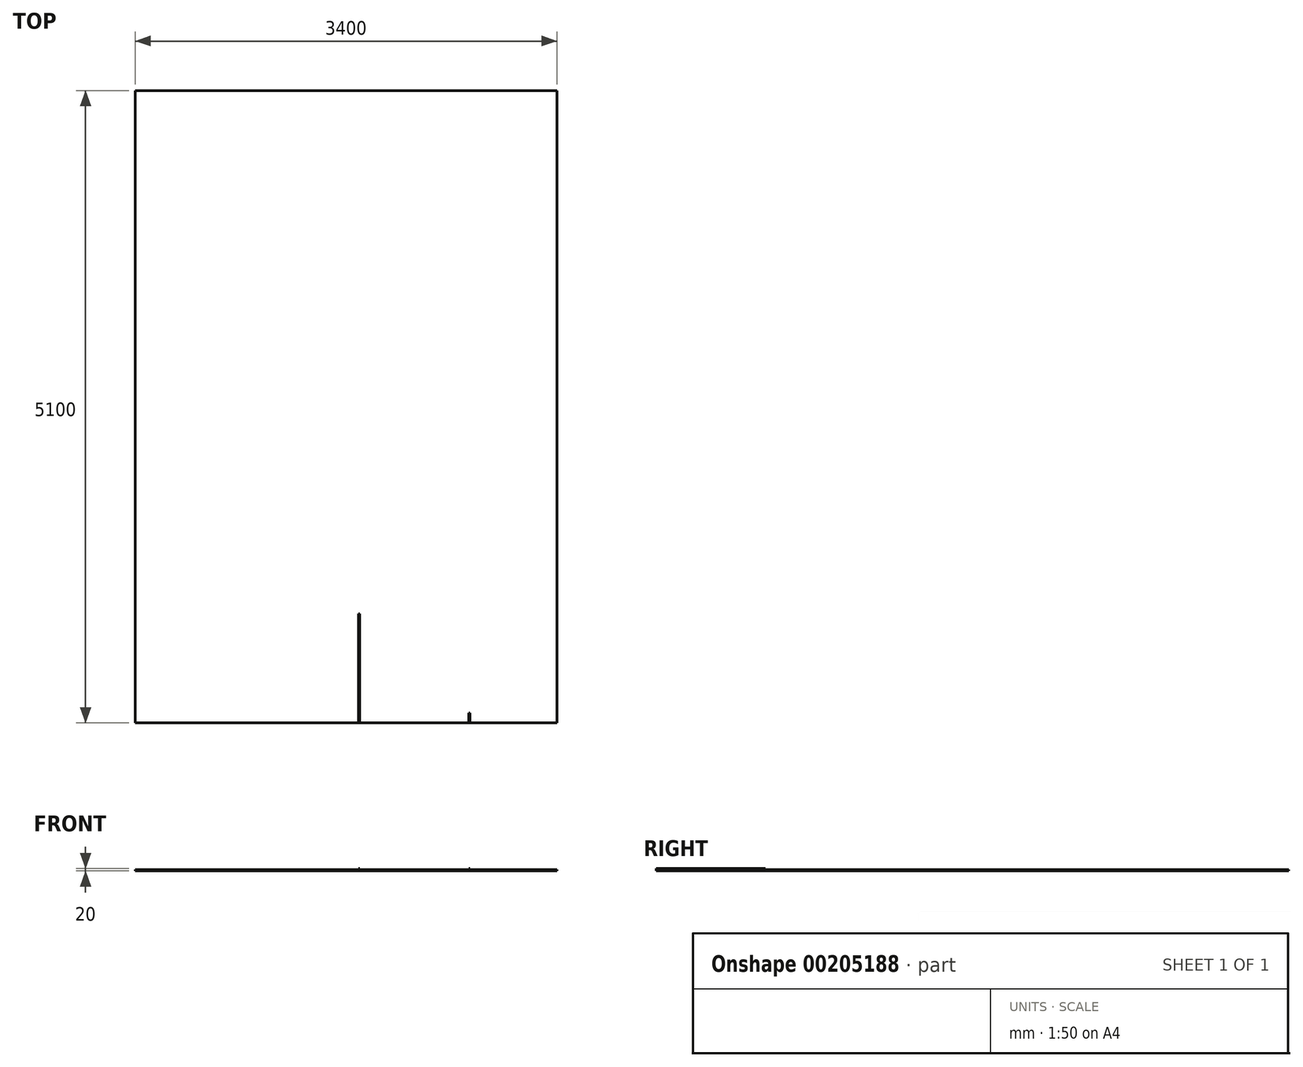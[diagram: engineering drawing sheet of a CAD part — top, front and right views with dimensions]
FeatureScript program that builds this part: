
annotation { "Feature Type Name" : "Feature", "Feature Type Description" : "" }
export const myFeature = defineFeature(function(context is Context, id is Id, definition is map)
    precondition{}
    {
        {
            var Q0;
            Q0=qCreatedBy(makeId("Top.planeOp"),FACE);
            var sketch = newSketch(context, id + "F0", { "sketchPlane" : qUnion([Q0])});
            skLineSegment(sketch, "E0.bottom", {"start": v(1700, 2550) * mm, "end": v(-1700, 2550) * mm});
            skLineSegment(sketch, "E0.top", {"start": v(1700, -2550) * mm, "end": v(-1700, -2550) * mm});
            skLineSegment(sketch, "E0.left", {"start": v(1700, 2550) * mm, "end": v(1700, -2550) * mm});
            skLineSegment(sketch, "E0.right", {"start": v(-1700, 2550) * mm, "end": v(-1700, -2550) * mm});
            skPoint(sketch, "E0.middle", {"position": v(0, 0) * mm});
            skSolve(sketch);
        }
        {
            var Q0;
            Q0 = qSketchRegion(id + "F0", true);
            extrude(context, id + "F1", {"entities" : qUnion([Q0]), "depth" : 10 * mm});
        }
        {
            var Q0;
            Q0=makeQuery(id+"F1.opExtrude","CAP_FACE",FACE,{"disambiguationData":[OSD([sQuery(id+"F0.wireOp",EDGE,"E0.bottom"),sQuery(id+"F0.wireOp",EDGE,"E0.top"),sQuery(id+"F0.wireOp",EDGE,"E0.left"),sQuery(id+"F0.wireOp",EDGE,"E0.right")])],"isStart":false});
            var sketch = newSketch(context, id + "F2", { "sketchPlane" : qUnion([Q0])});
            skLineSegment(sketch, "E1", {"start": v(1000, -2550) * mm, "end": v(1000, -2470) * mm});
            skLineSegment(sketch, "E2", {"start": v(1000, -2470) * mm, "end": v(990, -2470) * mm});
            skLineSegment(sketch, "E3", {"start": v(990, -2470) * mm, "end": v(990, -2550) * mm});
            skLineSegment(sketch, "E4", {"start": v(990, -2550) * mm, "end": v(1000, -2550) * mm});
            skLineSegment(sketch, "E5", {"start": v(110, -2550) * mm, "end": v(110, -2470) * mm});
            skLineSegment(sketch, "E6", {"start": v(110, -2470) * mm, "end": v(100, -2470) * mm});
            skLineSegment(sketch, "E7", {"start": v(100, -2470) * mm, "end": v(100, -2550) * mm});
            skLineSegment(sketch, "E8", {"start": v(100, -2550) * mm, "end": v(110, -2550) * mm});
            skArc(sketch, "E9.0", {"start": v(995, -2550) * mm, "mid": v(994.1, -2509.96) * mm, "end": v(991.38, -2470) * mm});
            skLineSegment(sketch, "E10", {"start": v(100, -2470) * mm, "end": v(100, -1670) * mm});
            skLineSegment(sketch, "E11", {"start": v(100, -1670) * mm, "end": v(110, -1670) * mm});
            skLineSegment(sketch, "E12", {"start": v(110, -1670) * mm, "end": v(110, -2470) * mm});
            skSolve(sketch);
        }
        {
            var Q0;
            Q0 = qSketchRegion(id + "F2", true);
            extrude(context, id + "F3", {"entities" : qUnion([Q0]), "operationType" : NewBodyOperationType.ADD, "depth" : 10 * mm});
        }
    });
